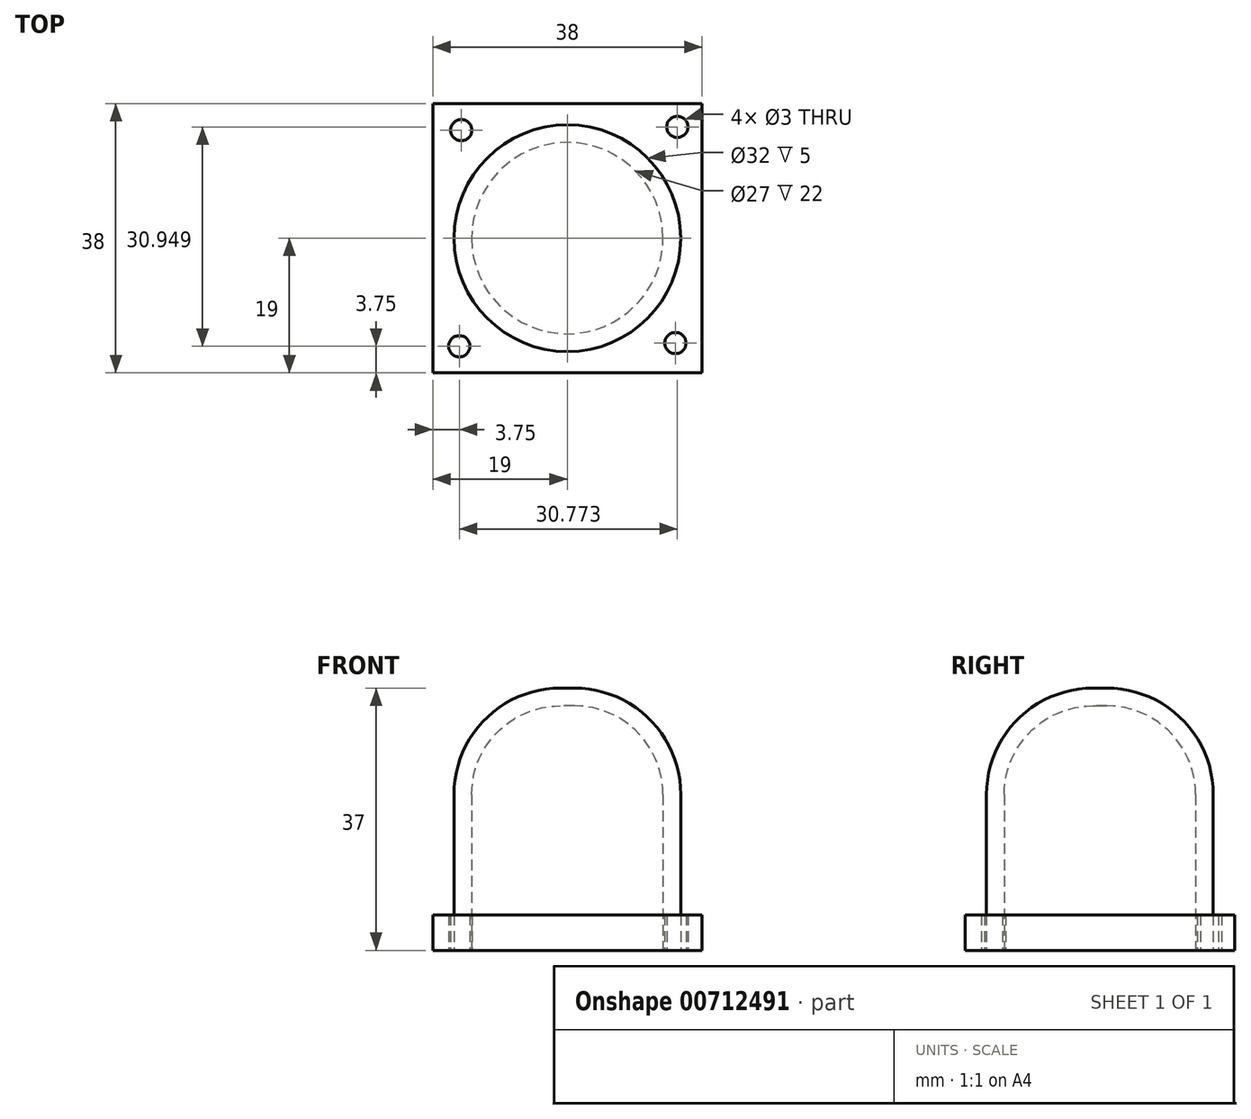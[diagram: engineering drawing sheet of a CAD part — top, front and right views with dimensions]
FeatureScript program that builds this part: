
annotation { "Feature Type Name" : "Feature", "Feature Type Description" : "" }
export const myFeature = defineFeature(function(context is Context, id is Id, definition is map)
    precondition{}
    {
        {
            var Q0;
            Q0=qCreatedBy(makeId("Top.planeOp"),FACE);
            var sketch = newSketch(context, id + "F0", { "sketchPlane" : qUnion([Q0])});
            skLineSegment(sketch, "E0.bottom", {"start": v(0, 0) * mm, "end": v(38, 0) * mm});
            skLineSegment(sketch, "E0.top", {"start": v(0, 38) * mm, "end": v(38, 38) * mm});
            skLineSegment(sketch, "E0.left", {"start": v(0, 0) * mm, "end": v(0, 38) * mm});
            skLineSegment(sketch, "E0.right", {"start": v(38, 0) * mm, "end": v(38, 38) * mm});
            skCircle(sketch, "E1", {"center": v(19, 19) * mm, "radius": 16 * mm});
            skCircle(sketch, "E2", {"center": v(4.02, 34.25) * mm, "radius": 1.5 * mm});
            skCircle(sketch, "E3", {"center": v(34.52, 34.7) * mm, "radius": 1.5 * mm});
            skCircle(sketch, "E4", {"center": v(34.25, 4.2) * mm, "radius": 1.5 * mm});
            skCircle(sketch, "E5", {"center": v(3.75, 3.75) * mm, "radius": 1.5 * mm});
            skSolve(sketch);
        }
        {
            var Q0;
            Q0=makeQuery(id+"F0.imprint","IMPRINT",FACE,{"disambiguationData":[TD([[makeQuery(id+"F0.imprint","IMPRINT",EDGE,{"derivedFrom":sQuery(id+"F0.wireOp",EDGE,"E1")}),1.0]])]});
            var Q1;
            Q1=sQuery(id+"F0.wireOp",EDGE,"E1");
            extrude(context, id + "F1", {"entities" : qUnion([Q0]), "surfaceEntities" : qUnion([Q1]), "depth" : 37 * mm, "offsetDistance" : 25 * mm});
        }
        {
            var Q0;
            Q0 = qSketchRegion(id + "F0", true);
            extrude(context, id + "F2", {"entities" : qUnion([Q0]), "depth" : 5 * mm, "offsetDistance" : 25 * mm});
        }
        {
            var Q0;
            Q0=makeQuery(id+"F1.opExtrude","CAP_EDGE",EDGE,{"disambiguationData":[OSD([sQuery(id+"F0.wireOp",EDGE,"E1")])],"isStart":false});
            fillet(context, id + "F3", {"entities" : qUnion([Q0]), "radius" : 15 * mm, "tangentPropagation" : true, "allowEdgeOverflow" : false});
        }
        {
            var Q0;
            Q0=makeQuery(id+"F1.opExtrude","CAP_FACE",FACE,{"disambiguationData":[OSD([sQuery(id+"F0.wireOp",EDGE,"E1")])],"isStart":true});
            shell(context, id + "F4", {"entities" : qUnion([Q0]), "thickness" : 2.5 * mm});
        }
    });
